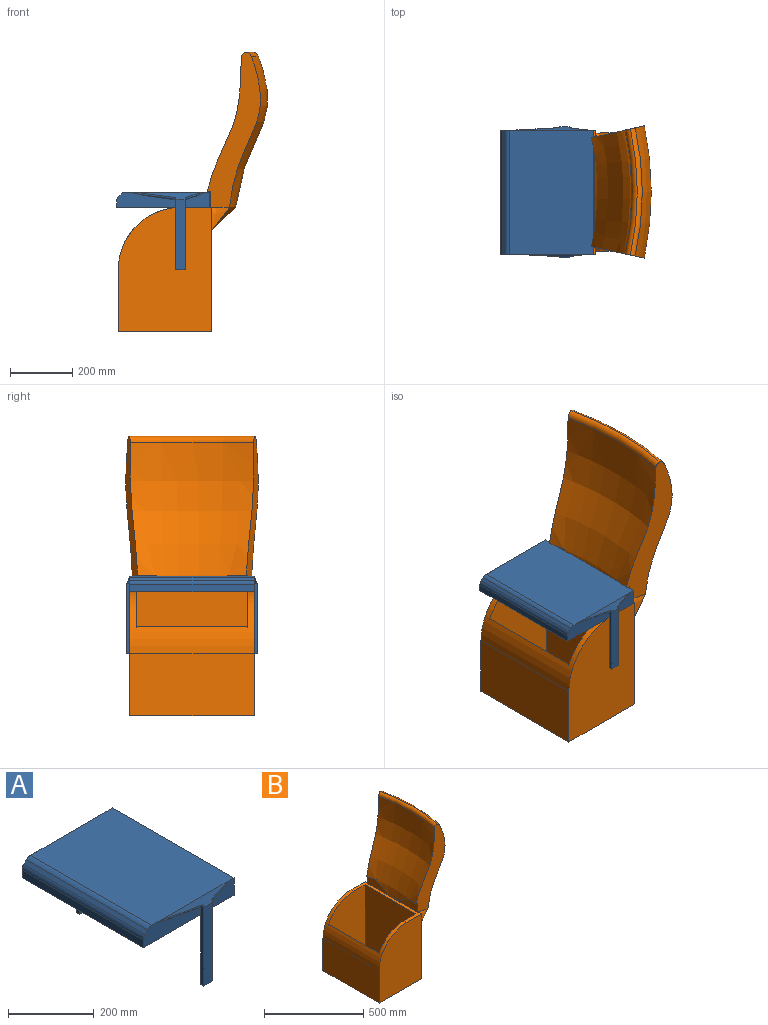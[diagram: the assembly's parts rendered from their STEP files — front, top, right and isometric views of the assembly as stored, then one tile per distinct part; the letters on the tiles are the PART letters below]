
ASSEMBLY  parts=2 mates=1
PART A: 31 faces, bbox 301.2x423.1x256.8 mm
  f0: plane 80x50mm, normal (0,-1,0), area 3110.5mm2, adj f3,f4,f5,f7,f12,f14
  f1: plane 190x50mm, normal (0,-1,0), area 7153.2mm2, adj f2,f3,f5,f8,f13,f15,f28,f29
  f2: plane 400x21.72mm, normal (-1,0,0), area 8686.3mm2, adj f1,f3,f17,f30
  f3: plane 400x300mm, normal (0,0,-1), area 120000mm2, adj f0,f1,f2,f4,f6,f16,f17,f18
  f4: plane 400x50mm, normal (1,0,0), area 20000mm2, adj f0,f3,f5,f16
  f5: plane 400x271.72mm, normal (0,0,1), area 108686.3mm2, adj f0,f1,f4,f11,f16,f17,f23,f29
  f6: plane 199.8x30mm, normal (0,1,0), area 5993.8mm2, adj f3,f7,f8,f9
  f7: plane 233.34x11.23mm, normal (1,0,0), area 2262.7mm2, adj f0,f6,f9,f10,f11,f12,f14
  f8: plane 232.3x10.57mm, normal (-1,0,0), area 2260.4mm2, adj f1,f6,f9,f10,f11,f13,f15
  f9: plane 30x10mm, normal (0,0,-1), area 300mm2, adj f6,f7,f8,f10
  f10: plane 225.61x30.01mm, normal (0,-1,0), area 6757.2mm2, adj f7,f8,f9,f11
  f11: bspline ~300x25mm, area 2682.6mm2, adj f5,f7,f8,f10,f14,f15
  f12: plane 21.77x6.75mm, normal (0.3,0,-0.96), area 31.5mm2, adj f0,f7,f14
  f13: plane 51.71x6.8mm, normal (-0.13,0,-0.99), area 73.3mm2, adj f1,f8,f15
  f14: bspline ~86.81x32.85mm, area 496.6mm2, adj f0,f7,f11,f12
  f15: bspline ~178.84x30.24mm, area 1150.2mm2, adj f1,f8,f11,f13
  f16: plane 80x50mm, normal (0,1,0), area 3110.5mm2, adj f3,f4,f5,f19,f24,f26
  f17: plane 190x50mm, normal (0,1,0), area 7153.2mm2, adj f2,f3,f5,f20,f25,f27,f28,f29
  f18: plane 199.8x30mm, normal (0,-1,0), area 5993.8mm2, adj f3,f19,f20,f21
  f19: plane 233.34x11.23mm, normal (1,0,0), area 2262.7mm2, adj f16,f18,f21,f22,f23,f24,f26
  f20: plane 232.3x10.57mm, normal (-1,0,0), area 2260.4mm2, adj f17,f18,f21,f22,f23,f25,f27
  f21: plane 30x10mm, normal (0,0,-1), area 300mm2, adj f18,f19,f20,f22
  f22: plane 225.61x30.01mm, normal (0,1,0), area 6757.2mm2, adj f19,f20,f21,f23
  f23: bspline ~300x25mm, area 2682.6mm2, adj f5,f19,f20,f22,f26,f27
  f24: plane 21.77x6.75mm, normal (0.3,0,-0.96), area 31.5mm2, adj f16,f19,f26
  f25: plane 51.71x6.8mm, normal (-0.13,0,-0.99), area 73.3mm2, adj f17,f20,f27
  f26: bspline ~86.81x32.85mm, area 496.6mm2, adj f16,f19,f23,f24
  f27: bspline ~178.84x30.24mm, area 1150.2mm2, adj f17,f20,f23,f25
  f28: plane 400x8.28mm, normal (-0.71,0,0.71), area 4686.3mm2, adj f1,f17,f29,f30
  f29: cylinder r=20mm len=400mm, axis (0,-1,0), area 6283.2mm2, adj f1,f5,f17,f28
  f30: cylinder r=20mm len=400mm, axis (0,-1,0), area 6283.2mm2, adj f1,f2,f17,f28
PART B: 28 faces, bbox 550.8x467.4x920 mm
  f0: revolved ~479.94x398.32mm, area 177889.5mm2, adj f2,f4,f5,f6,f7,f8,f27
  f1: plane 357.7x3.95mm, normal (0,0,-1), area 1410.4mm2, adj f2,f4,f9,f24
  f2: plane 499.86x187.51mm, normal (-0.22,-0.98,0), area 33518.1mm2, adj f0,f1,f3,f7,f8,f10,f21,f25
  f3: revolved ~480.24x425.76mm, area 206500.8mm2, adj f2,f4,f25,f26
  f4: plane 499.86x187.51mm, normal (-0.22,0.98,0), area 33518.1mm2, adj f0,f1,f3,f5,f6,f10,f23,f25
  f5: plane 58.58x10.4mm, normal (0,0,-1), area 285.4mm2, adj f0,f4,f6
  f6: plane 197.39x72.02mm, normal (-1,0,0), area 5382.8mm2, adj f0,f4,f5,f10
  f7: plane 197.38x72.02mm, normal (-1,0,0), area 5382.8mm2, adj f0,f2,f8,f10
  f8: plane 58.58x10.4mm, normal (0,0,-1), area 285.4mm2, adj f0,f2,f7
  f9: plane 400x400mm, normal (1,0,0), area 132970.3mm2, adj f1,f10,f12,f14,f15,f21,f22,f23
  f10: plane 400x100mm, normal (0,0,1), area 10210.3mm2, adj f2,f4,f6,f7,f9,f11,f14,f15
  f11: cylinder r=200mm len=400mm, axis (0,1,0), area 45040.3mm2, adj f10,f13,f14,f15,f16,f17,f18
  f12: plane 400x300mm, normal (0,0,-1), area 120000mm2, adj f9,f13,f14,f15
  f13: plane 400x200mm, normal (-1,0,0), area 80000mm2, adj f11,f12,f14,f15
  f14: plane 400x300mm, normal (0,-1,0), area 111415.9mm2, adj f9,f10,f11,f12,f13
  f15: plane 400x300mm, normal (0,1,0), area 111415.9mm2, adj f9,f10,f11,f12,f13
  f16: plane 380x260mm, normal (0,1,0), area 93041.4mm2, adj f10,f11,f18,f19,f20
  f17: plane 380x260mm, normal (0,-1,0), area 93041.4mm2, adj f10,f11,f18,f19,f20
  f18: plane 360x267.18mm, normal (1,0,0), area 96184.1mm2, adj f11,f16,f17,f20
  f19: plane 380x360mm, normal (-1,0,0), area 136800mm2, adj f10,f16,f17,f20
  f20: plane 360x260mm, normal (0,0,1), area 93600mm2, adj f16,f17,f18,f19
  f21: bspline ~73.84x58.05mm, area 2232.4mm2, adj f2,f9,f22,f24,f25
  f22: bspline ~381.75x78.95mm, area 36418.2mm2, adj f9,f21,f23,f25
  f23: bspline ~73.84x58.05mm, area 2229.1mm2, adj f4,f9,f22,f24,f25
  f24: plane 381.55x3.95mm, normal (-0.6,0,0.8), area 1834.7mm2, adj f1,f9,f21,f23
  f25: bspline ~387.94x26.83mm, area 6337.8mm2, adj f2,f3,f4,f21,f22,f23
  f26: torus R=934.85mm, axis (0,0,-1), area 8834.9mm2, adj f2,f3,f4,f27
  f27: torus R=940.16mm, axis (0,0,-1), area 11644.3mm2, adj f0,f2,f4,f26
PLACE A rot(axis=(0.01,-1,-0.06),0deg) t=(-36.71,-23.46,26.25)mm
PLACE B t=(277.41,-23.46,43.35)mm fixed
MATE revolute A.f6 <-> B.f11  axis (0,1,0) through (180.2,-223.46,-156.65)mm
